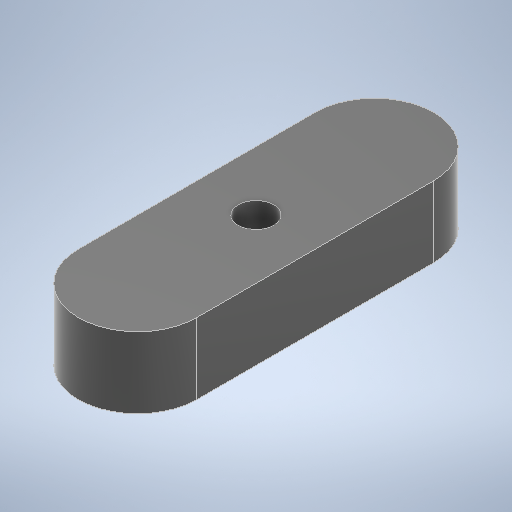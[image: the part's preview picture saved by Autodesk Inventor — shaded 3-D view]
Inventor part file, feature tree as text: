
AUTODESK INVENTOR PART (.ipt)
format: ipt  version: 2025.1 (Build 291241020, 241B)  size: 546,816 bytes
history: native  units: mm
features: sketch x2, extrude x1, hole x1, fillet x1
ambient origin geometry x8: Origin, YZ Plane, XZ Plane, XY Plane, X Axis, Y Axis, Z Axis, Center Point
bodies: Solid1 (feature_tree)
feature tree (5):
  extrude  "Extrusion1"  Depth=20.0mm
  hole  "Hole1"  [1 undecoded]
  fillet  "Fillet1"  Radius=30.0mm
  sketch  "Sketch1"  dims[d0=60.0mm d1=20.0mm]
  sketch  "Sketch2"  dims[d2=12.0mm d3=0.0mm d5=10.0mm d6=30.0mm d7=6.0mm d8=6.0mm d9=4.0mm d10=2.0mm d11=90.0deg d12=8.0mm d13=20.594885mm d14=10.0mm]
note: 1 required parameter value undecoded (feature->parameter linkage not recoverable at this tier; creation-order binding heuristic only, values carry confidence <= 0.55)
